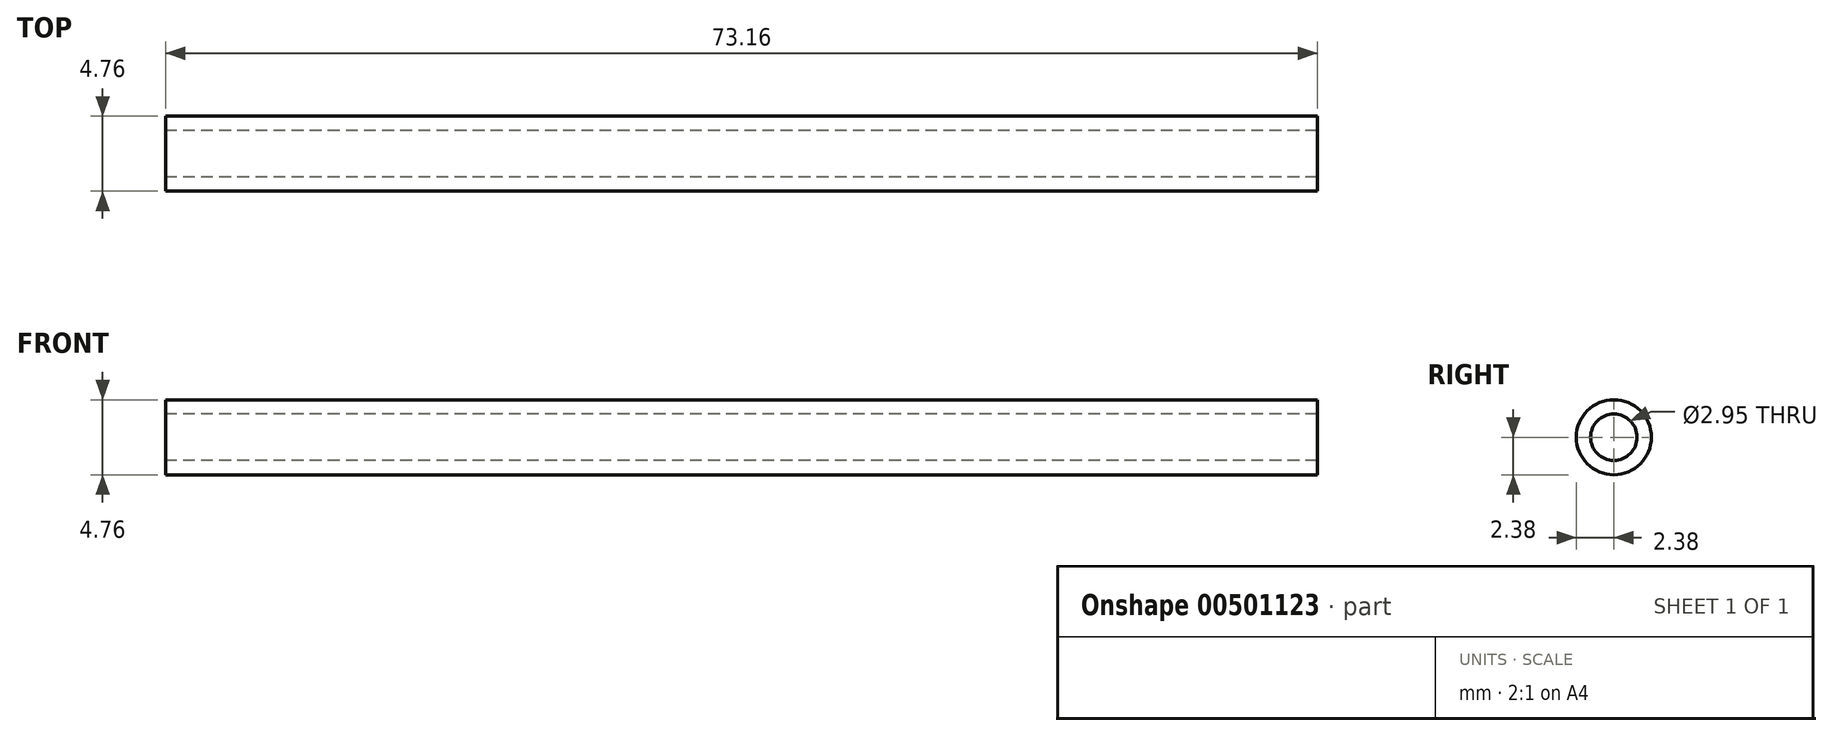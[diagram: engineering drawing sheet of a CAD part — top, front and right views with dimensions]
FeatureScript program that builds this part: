
annotation { "Feature Type Name" : "Feature", "Feature Type Description" : "" }
export const myFeature = defineFeature(function(context is Context, id is Id, definition is map)
    precondition{}
    {
        {
            var Q0;
            Q0=qCreatedBy(makeId("Right.planeOp"),FACE);
            var sketch = newSketch(context, id + "F0", { "sketchPlane" : qUnion([Q0])});
            skCircle(sketch, "E0", {"center": v(0, 0) * mm, "radius": 2.38 * mm});
            skCircle(sketch, "E1", {"center": v(0, 0) * mm, "radius": 1.47 * mm});
            skSolve(sketch);
        }
        {
            var Q0;
            Q0=qSketchRegion(id+"F0",true);
            extrude(context, id + "F1", {"entities" : qUnion([Q0]), "depth" : 73.15 * mm, "symmetric" : true});
        }
    });
